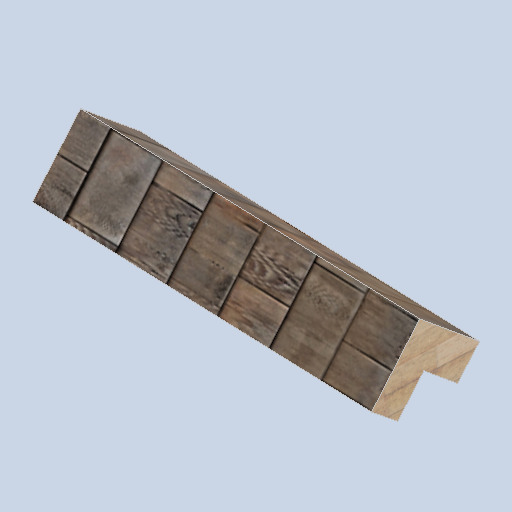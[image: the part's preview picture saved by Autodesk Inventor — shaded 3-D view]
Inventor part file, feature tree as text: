
AUTODESK INVENTOR PART (.ipt)
format: ipt  version: 2024.2 (Build 282272000, 272)  size: 245,248 bytes
history: native  units: in
note: dims shown in document units (in); Inventor stores cm internally (conversion verified against a paired STEP export)
features: sketch x8, plane x5, other x3
ambient origin geometry x8: Origin, YZ Plane, XZ Plane, XY Plane, X Axis, Y Axis, Z Axis, Center Point
bodies: Solid1 (feature_tree)
feature tree (16):
  other  "panel_pad_frame_02.ipt"
  other  "Solid1::panel_pad_frame_02.ipt"
  other  "TaggingFeature1"
  sketch  "Sketch1"  dims[d0=0.3937in]
  sketch  "Sketch2"
  sketch  "Sketch3"
  sketch  "Sketch6"
  sketch  "Sketch7"
  sketch  "Sketch8"
  sketch  "Sketch9"
  sketch  "Sketch10"
  plane  "Work Plane1"
  plane  "Work Plane2"
  plane  "Work Plane3"
  plane  "Work Plane4"
  plane  "Work Plane5"
